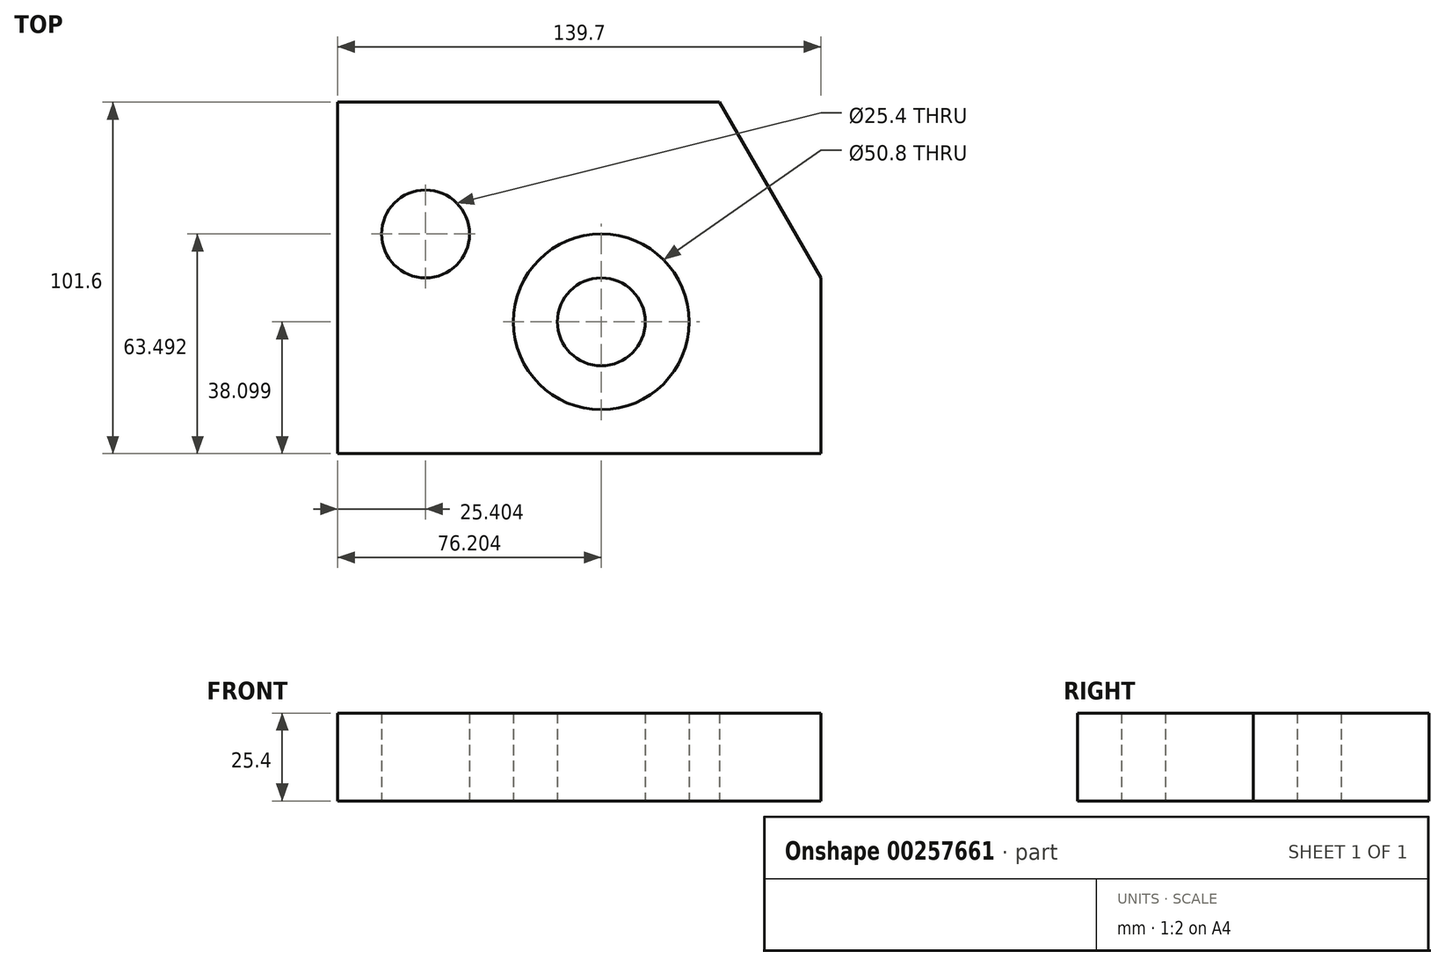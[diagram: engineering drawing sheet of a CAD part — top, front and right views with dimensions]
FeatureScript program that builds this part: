
annotation { "Feature Type Name" : "Feature", "Feature Type Description" : "" }
export const myFeature = defineFeature(function(context is Context, id is Id, definition is map)
    precondition{}
    {
        {
            var Q0;
            Q0=qCreatedBy(makeId("Top.planeOp"),FACE);
            var sketch = newSketch(context, id + "F0", { "sketchPlane" : qUnion([Q0])});
            skLineSegment(sketch, "E0", {"start": v(-43.7, -58.03) * mm, "end": v(96, -58.03) * mm});
            skLineSegment(sketch, "E1", {"start": v(96, -58.03) * mm, "end": v(96, -7.23) * mm});
            skLineSegment(sketch, "E2", {"start": v(66.67, 43.57) * mm, "end": v(-43.7, 43.57) * mm});
            skLineSegment(sketch, "E3", {"start": v(-43.7, 43.57) * mm, "end": v(-43.7, -58.03) * mm});
            skLineSegment(sketch, "E4", {"start": v(96, -7.23) * mm, "end": v(66.67, 43.57) * mm});
            skLineSegment(sketch, "E5", {"start": v(-43.7, -58.03) * mm, "end": v(-43.7, 5.46) * mm});
            skCircle(sketch, "E6", {"center": v(-18.3, 5.46) * mm, "radius": 12.7 * mm});
            skLineSegment(sketch, "E7", {"start": v(-43.7, -58.03) * mm, "end": v(32.5, -58.03) * mm});
            skCircle(sketch, "E8", {"center": v(32.5, -19.93) * mm, "radius": 25.4 * mm});
            skCircle(sketch, "E9", {"center": v(32.5, -19.93) * mm, "radius": 12.7 * mm});
            skSolve(sketch);
        }
        {
            var Q0;
            Q0 = qSketchRegion(id + "F0", true);
            var Q1;
            Q1=makeQuery(id+"F0.imprint","IMPRINT",FACE,{"disambiguationData":[TD([[makeQuery(id+"F0.imprint","IMPRINT",EDGE,{"derivedFrom":sQuery(id+"F0.wireOp",EDGE,"E9")}),1.0]])]});
            extrude(context, id + "F1", {"entities" : qUnion([Q0, Q1]), "depth" : 25.4 * mm});
        }
    });
